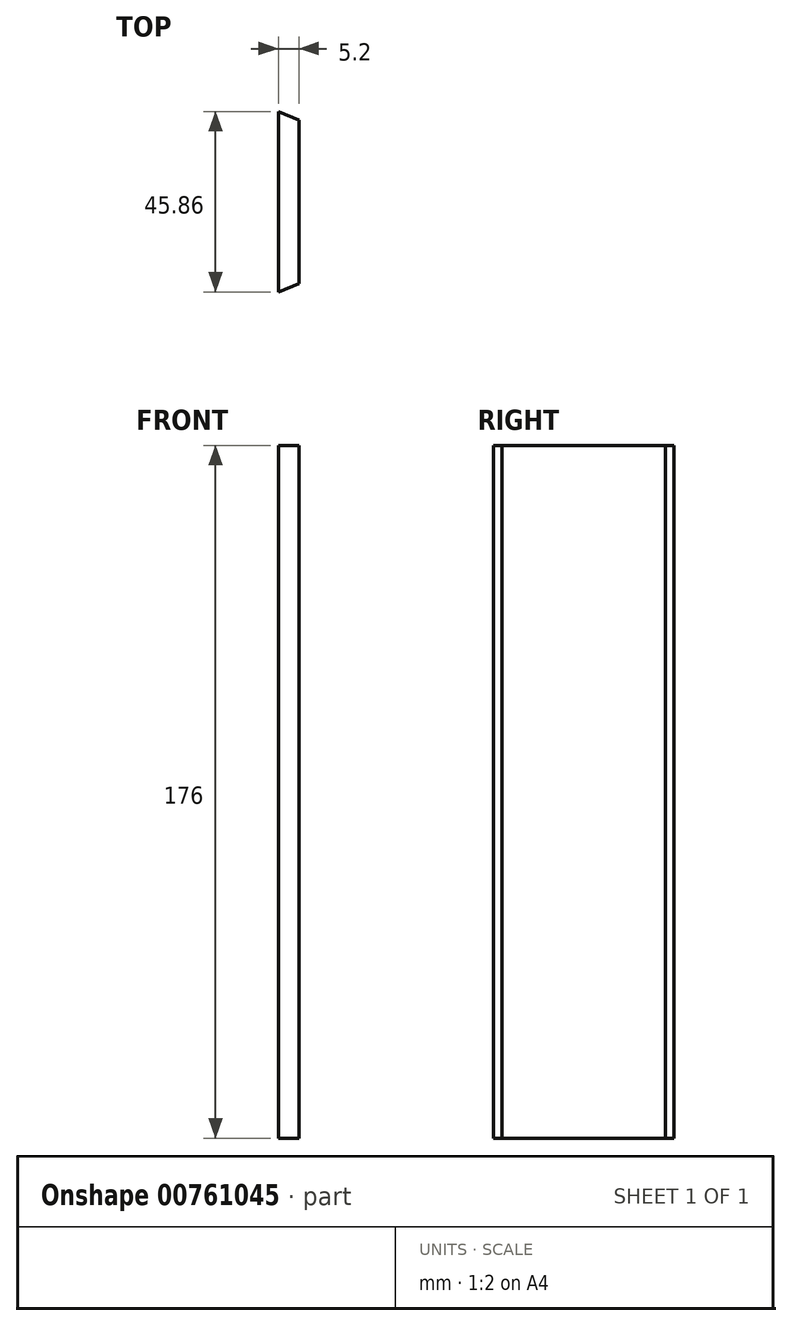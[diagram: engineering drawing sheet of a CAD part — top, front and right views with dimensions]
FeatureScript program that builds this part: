
annotation { "Feature Type Name" : "Feature", "Feature Type Description" : "" }
export const myFeature = defineFeature(function(context is Context, id is Id, definition is map)
    precondition{}
    {
        {
            var Q0;
            Q0=qCreatedBy(makeId("Top.planeOp"),FACE);
            var sketch = newSketch(context, id + "F0", { "sketchPlane" : qUnion([Q0])});
            skLineSegment(sketch, "E0.5", {"start": v(-55.5, 23.97) * mm, "end": v(-55.5, -21.9) * mm});
            skLineSegment(sketch, "E1.5", {"start": v(-50.3, 21.81) * mm, "end": v(-50.3, -19.74) * mm});
            skLineSegment(sketch, "E2", {"start": v(-55.5, 23.97) * mm, "end": v(-50.3, 21.81) * mm});
            skLineSegment(sketch, "E3", {"start": v(-50.3, -19.74) * mm, "end": v(-55.5, -21.9) * mm});
            skSolve(sketch);
        }
        {
            var Q0;
            Q0 = qSketchRegion(id + "F0", true);
            extrude(context, id + "F1", {"entities" : qUnion([Q0]), "depth" : 176 * mm, "offsetDistance" : 25 * mm});
        }
    });
